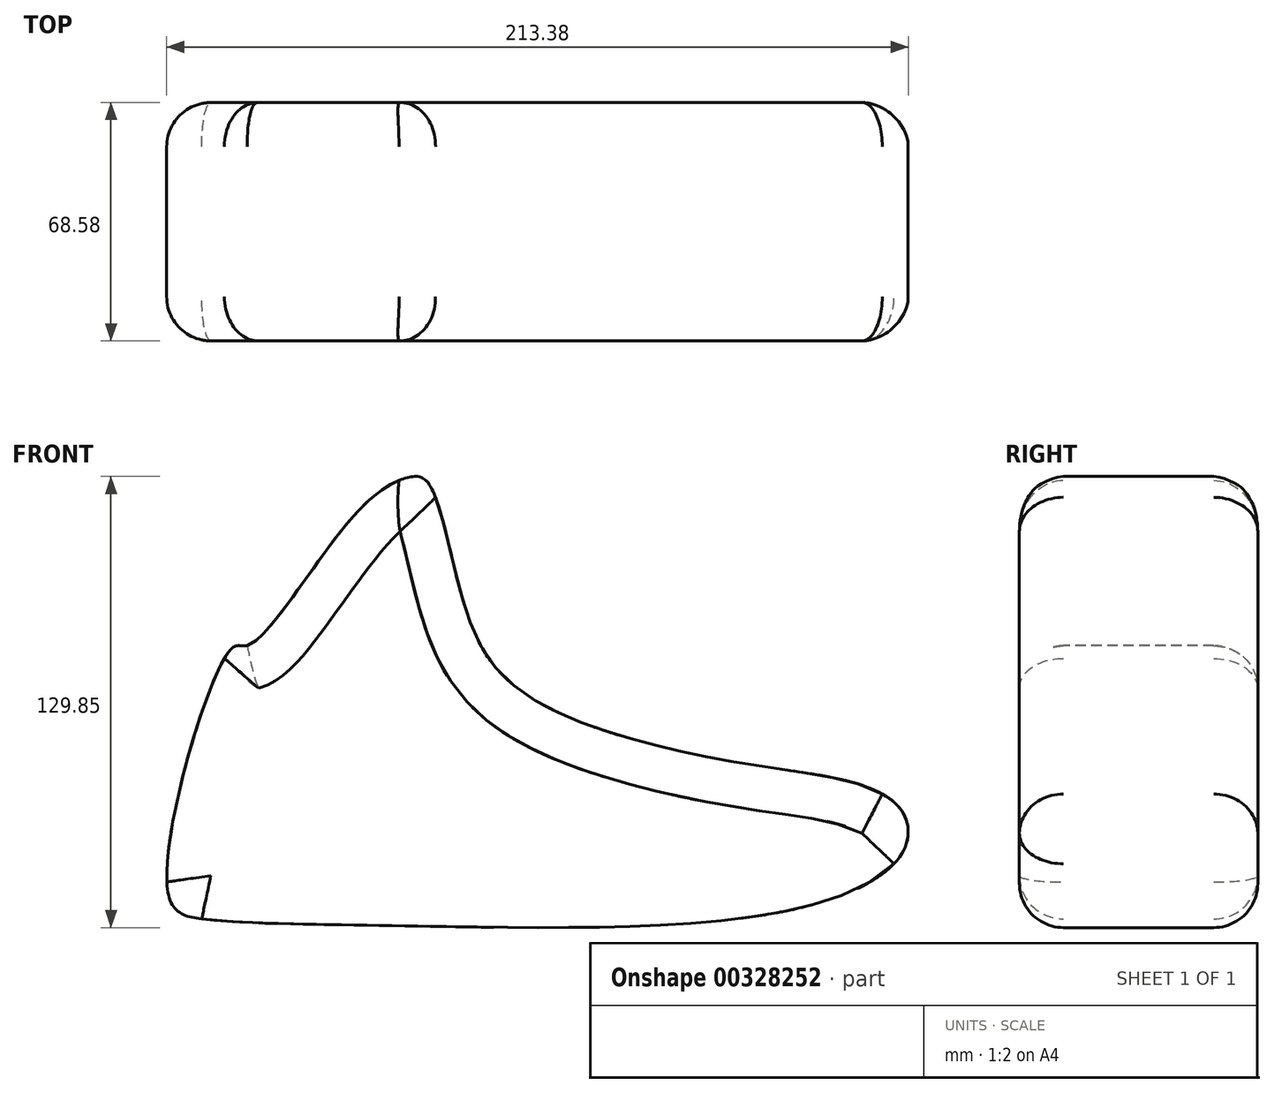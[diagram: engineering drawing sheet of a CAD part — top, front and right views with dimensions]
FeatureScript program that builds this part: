
annotation { "Feature Type Name" : "Feature", "Feature Type Description" : "" }
export const myFeature = defineFeature(function(context is Context, id is Id, definition is map)
    precondition{}
    {
        {
            var Q0;
            Q0=qCreatedBy(makeId("Front.planeOp"),FACE);
            var sketch = newSketch(context, id + "F0", { "sketchPlane" : qUnion([Q0])});
            skFitSpline(sketch, "E0", {"points": [v(-52.75, 71.26) * mm, v(-83.1, 33.79) * mm, v(-88.05, 32.86) * mm, v(-106.63, -36.5) * mm, v(-95.8, -45.18) * mm, v(-39.43, -47.04) * mm, v(71.73, -42.7) * mm, v(104.86, -25.98) * mm, v(104.86, -14.21) * mm, v(90.93, -5.85) * mm, v(57.18, 0) * mm, v(-3.51, 19.54) * mm, v(-22.1, 48.34) * mm, v(-31.7, 80.55) * mm, v(-36.96, 82.1) * mm, v(-52.75, 71.26) * mm]});
            skFitSpline(sketch, "E1", {"points": [v(51.33, 68.27) * mm, v(51.54, 71.3) * mm], "startDerivative": vector(0.21, 3.04) * mm, "endDerivative": vector(0.21, 3.04) * mm});
            skSolve(sketch);
        }
        {
            var Q0;
            Q0 = qSketchRegion(id + "F0", true);
            extrude(context, id + "F1", {"entities" : qUnion([Q0]), "depth" : 68.58 * mm});
        }
        {
            var Q0;
            Q0=makeQuery(id+"F1.opExtrude","CAP_EDGE",EDGE,{"disambiguationData":[OSD([sQuery(id+"F0.wireOp",EDGE,"E0")])],"isStart":false});
            var Q1;
            Q1=makeQuery(id+"F1.opExtrude","CAP_EDGE",EDGE,{"disambiguationData":[OSD([sQuery(id+"F0.wireOp",EDGE,"E0")])],"isStart":true});
            fillet(context, id + "F2", {"entities" : qUnion([Q0, Q1]), "radius" : 12.7 * mm, "tangentPropagation" : true, "allowEdgeOverflow" : false});
        }
    });
